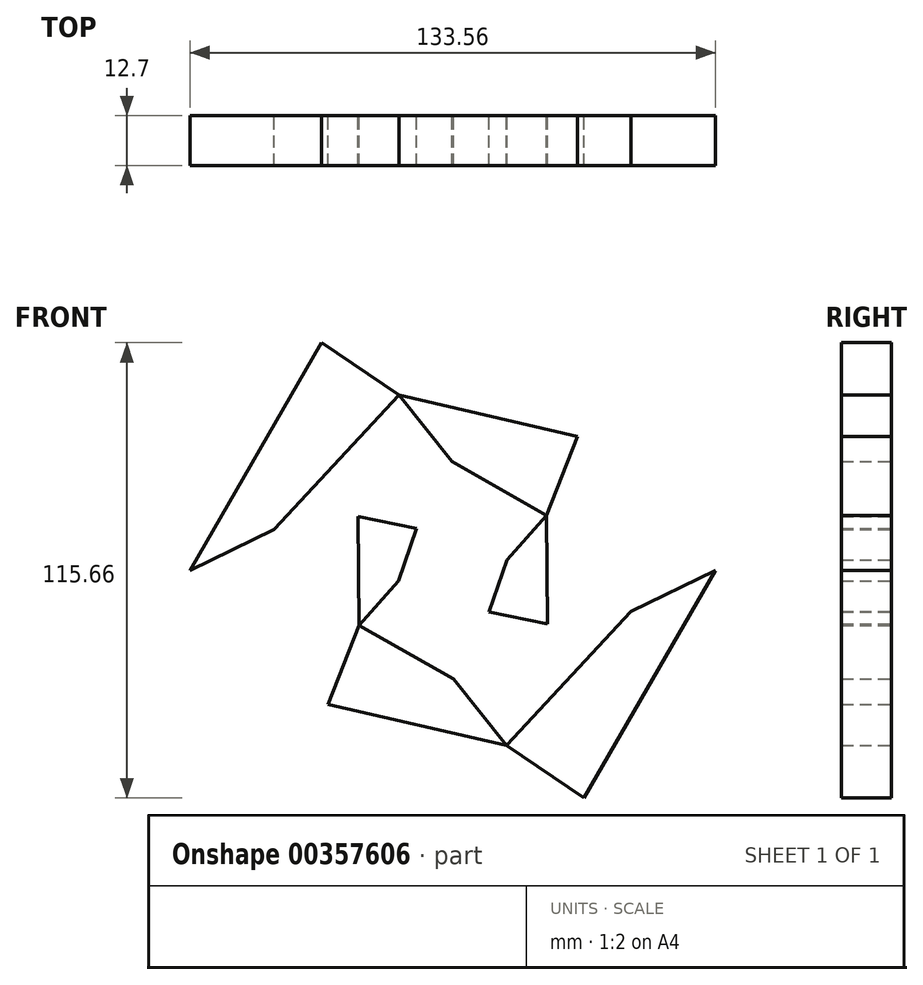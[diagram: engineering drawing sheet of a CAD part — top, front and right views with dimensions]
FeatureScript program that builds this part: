
annotation { "Feature Type Name" : "Feature", "Feature Type Description" : "" }
export const myFeature = defineFeature(function(context is Context, id is Id, definition is map)
    precondition{}
    {
        {
            var Q0;
            Q0=qCreatedBy(makeId("Front.planeOp"),FACE);
            var sketch = newSketch(context, id + "F0", { "sketchPlane" : qUnion([Q0])});
            skCircle(sketch, "E0.cCircle", {"center": v(0, 0) * mm, "radius": 57.83 * mm, "construction": true});
            skLineSegment(sketch, "E0.0", {"start": v(66.78, 0) * mm, "end": v(33.39, -57.83) * mm});
            skLineSegment(sketch, "E0.1", {"start": v(33.39, -57.83) * mm, "end": v(-33.39, -57.83) * mm});
            skLineSegment(sketch, "E0.2", {"start": v(-33.39, -57.83) * mm, "end": v(-66.78, 0) * mm});
            skLineSegment(sketch, "E0.3", {"start": v(-66.78, 0) * mm, "end": v(-33.39, 57.83) * mm});
            skLineSegment(sketch, "E0.4", {"start": v(-33.39, 57.83) * mm, "end": v(33.39, 57.83) * mm});
            skLineSegment(sketch, "E0.5", {"start": v(33.39, 57.83) * mm, "end": v(66.78, 0) * mm});
            skPoint(sketch, "E0.0.midPoint", {"position": v(50.08, -28.92) * mm});
            skCircle(sketch, "E1.cCircle", {"center": v(0, 0) * mm, "radius": 40.29 * mm, "construction": true});
            skLineSegment(sketch, "E1.0", {"start": v(45.34, -10.43) * mm, "end": v(13.64, -44.48) * mm});
            skLineSegment(sketch, "E1.1", {"start": v(13.64, -44.48) * mm, "end": v(-31.7, -34.05) * mm});
            skLineSegment(sketch, "E1.2", {"start": v(-31.7, -34.05) * mm, "end": v(-45.34, 10.43) * mm});
            skLineSegment(sketch, "E1.3", {"start": v(-45.34, 10.43) * mm, "end": v(-13.64, 44.48) * mm});
            skLineSegment(sketch, "E1.4", {"start": v(-13.64, 44.48) * mm, "end": v(31.7, 34.05) * mm});
            skLineSegment(sketch, "E1.5", {"start": v(31.7, 34.05) * mm, "end": v(45.34, -10.43) * mm});
            skPoint(sketch, "E1.0.midPoint", {"position": v(29.49, -27.45) * mm});
            skLineSegment(sketch, "E2", {"start": v(-13.64, 44.48) * mm, "end": v(-33.39, 57.83) * mm});
            skLineSegment(sketch, "E3", {"start": v(31.7, 34.05) * mm, "end": v(33.39, 57.83) * mm});
            skLineSegment(sketch, "E4", {"start": v(45.34, -10.43) * mm, "end": v(66.78, 0) * mm});
            skLineSegment(sketch, "E5", {"start": v(13.64, -44.48) * mm, "end": v(33.39, -57.83) * mm});
            skLineSegment(sketch, "E6", {"start": v(-31.7, -34.05) * mm, "end": v(-33.39, -57.83) * mm});
            skLineSegment(sketch, "E7", {"start": v(-45.34, 10.43) * mm, "end": v(-66.78, 0) * mm});
            skCircle(sketch, "E8.cCircle", {"center": v(0, 0) * mm, "radius": 23.94 * mm, "construction": true});
            skLineSegment(sketch, "E8.0", {"start": v(24.02, -13.67) * mm, "end": v(0.17, -27.64) * mm});
            skLineSegment(sketch, "E8.1", {"start": v(0.17, -27.64) * mm, "end": v(-23.85, -13.97) * mm});
            skLineSegment(sketch, "E8.2", {"start": v(-23.85, -13.97) * mm, "end": v(-24.02, 13.67) * mm});
            skLineSegment(sketch, "E8.3", {"start": v(-24.02, 13.67) * mm, "end": v(-0.17, 27.64) * mm});
            skLineSegment(sketch, "E8.4", {"start": v(-0.17, 27.64) * mm, "end": v(23.85, 13.97) * mm});
            skLineSegment(sketch, "E8.5", {"start": v(23.85, 13.97) * mm, "end": v(24.02, -13.67) * mm});
            skPoint(sketch, "E8.0.midPoint", {"position": v(12.1, -20.66) * mm});
            skLineSegment(sketch, "E9", {"start": v(-13.64, 44.48) * mm, "end": v(-0.17, 27.64) * mm});
            skLineSegment(sketch, "E10", {"start": v(23.85, 13.97) * mm, "end": v(31.7, 34.05) * mm});
            skLineSegment(sketch, "E11", {"start": v(24.02, -13.67) * mm, "end": v(45.34, -10.43) * mm});
            skLineSegment(sketch, "E12", {"start": v(0.17, -27.64) * mm, "end": v(13.64, -44.48) * mm});
            skLineSegment(sketch, "E13", {"start": v(-23.85, -13.97) * mm, "end": v(-31.7, -34.05) * mm});
            skLineSegment(sketch, "E14", {"start": v(-24.02, 13.67) * mm, "end": v(-45.34, 10.43) * mm});
            skCircle(sketch, "E15.cCircle", {"center": v(0, 0) * mm, "radius": 12.18 * mm, "construction": true});
            skLineSegment(sketch, "E15.0", {"start": v(9.21, -10.63) * mm, "end": v(-4.6, -13.3) * mm});
            skLineSegment(sketch, "E15.1", {"start": v(-4.6, -13.3) * mm, "end": v(-13.8, -2.67) * mm});
            skLineSegment(sketch, "E15.2", {"start": v(-13.8, -2.67) * mm, "end": v(-9.21, 10.63) * mm});
            skLineSegment(sketch, "E15.3", {"start": v(-9.21, 10.63) * mm, "end": v(4.6, 13.3) * mm});
            skLineSegment(sketch, "E15.4", {"start": v(4.6, 13.3) * mm, "end": v(13.8, 2.67) * mm});
            skLineSegment(sketch, "E15.5", {"start": v(13.8, 2.67) * mm, "end": v(9.21, -10.63) * mm});
            skPoint(sketch, "E15.0.midPoint", {"position": v(2.31, -11.96) * mm});
            skLineSegment(sketch, "E16", {"start": v(-0.17, 27.64) * mm, "end": v(4.6, 13.3) * mm});
            skLineSegment(sketch, "E17", {"start": v(13.8, 2.67) * mm, "end": v(23.85, 13.97) * mm});
            skLineSegment(sketch, "E18", {"start": v(9.21, -10.63) * mm, "end": v(24.02, -13.67) * mm});
            skLineSegment(sketch, "E19", {"start": v(-4.6, -13.3) * mm, "end": v(0.17, -27.64) * mm});
            skLineSegment(sketch, "E20", {"start": v(-13.8, -2.67) * mm, "end": v(-23.85, -13.97) * mm});
            skLineSegment(sketch, "E21", {"start": v(-9.21, 10.63) * mm, "end": v(-24.02, 13.67) * mm});
            skSolve(sketch);
        }
        {
            var Q0;
            Q0=makeQuery(id+"F0.imprint","IMPRINT",FACE,{"disambiguationData":[TD([[makeQuery(id+"F0.imprint","IMPRINT",EDGE,{"derivedFrom":sQuery(id+"F0.wireOp",EDGE,"E1.4")}),-1.0]])]});
            var Q1;
            Q1=makeQuery(id+"F0.imprint","IMPRINT",FACE,{"disambiguationData":[TD([[makeQuery(id+"F0.imprint","IMPRINT",EDGE,{"derivedFrom":sQuery(id+"F0.wireOp",EDGE,"E8.5")}),-1.0]])]});
            var Q2;
            Q2=makeQuery(id+"F0.imprint","IMPRINT",FACE,{"disambiguationData":[TD([[makeQuery(id+"F0.imprint","IMPRINT",EDGE,{"derivedFrom":sQuery(id+"F0.wireOp",EDGE,"E8.2")}),-1.0]])]});
            var Q3;
            Q3=makeQuery(id+"F0.imprint","IMPRINT",FACE,{"disambiguationData":[TD([[makeQuery(id+"F0.imprint","IMPRINT",EDGE,{"derivedFrom":sQuery(id+"F0.wireOp",EDGE,"E1.1")}),-1.0]])]});
            var Q4;
            Q4=makeQuery(id+"F0.imprint","IMPRINT",FACE,{"disambiguationData":[TD([[makeQuery(id+"F0.imprint","IMPRINT",EDGE,{"derivedFrom":sQuery(id+"F0.wireOp",EDGE,"E0.3")}),-1.0]])]});
            var Q5;
            Q5=makeQuery(id+"F0.imprint","IMPRINT",FACE,{"disambiguationData":[TD([[makeQuery(id+"F0.imprint","IMPRINT",EDGE,{"derivedFrom":sQuery(id+"F0.wireOp",EDGE,"E0.0")}),-1.0]])]});
            extrude(context, id + "F1", {"entities" : qUnion([Q0, Q1, Q2, Q3, Q4, Q5]), "endBound" : BoundingType.SYMMETRIC, "depth" : 12.7 * mm});
        }
    });
